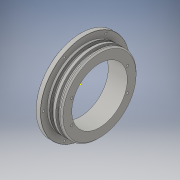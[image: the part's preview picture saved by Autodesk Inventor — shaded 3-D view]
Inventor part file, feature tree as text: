
AUTODESK INVENTOR PART (.ipt)
format: ipt  version: 2016 (Build 200138000, 138)  size: 337,408 bytes
history: native  units: in
note: dims shown in document units (in); Inventor stores cm internally (conversion verified against a paired STEP export)
features: sketch x5, extrude x3, chamfer x2, revolve x1, hole x1
ambient origin geometry x8: Origin, YZ Plane, XZ Plane, XY Plane, X Axis, Y Axis, Z Axis, Center Point
bodies: Solid1 (feature_tree)
feature tree (12):
  revolve  "Revolution1"  [1 undecoded]
  extrude  "Extrusion1"  Depth=0.13in
  extrude  "Extrusion2"  Depth=0.24in
  chamfer  "Chamfer1"  Distance=0.24in
  hole  "Hole1"  [1 undecoded]
  chamfer  "Chamfer2"  Distance=0.125in
  sketch  "Sketch8"  dims[d22=0.139in d23=0.0in d32=0.07in d33=0.125in d34=45.0deg]
  extrude  "Extrusion4"  Depth=0.995in
  sketch  "Sketch2"  dims[d2=0.175in d3=0.14in]
  sketch  "Sketch3"  dims[d4=0.175in d5=0.13in]
  sketch  "Sketch5"  dims[d8=90.0deg d10=4.65in d11=0.24in d12=0.0in]
  sketch  "Sketch9"  dims[d38=0.5in d42=0.125in d43=4.35in d44=2.3622in d46=360.0deg d48=0.1181in d49=0.75in d50=0.375in d51=0.25in d52=0.5635in d53=1.0in d54=0.8108in d55=0.01in d56=0.125in d57=45.0deg d62=3.819in d65=0.15in d66=0.15in d67=0.15in d68=0.055in d71=0.755in d72=1.68in d73=0.3in d74=0.3in d78=0.1181in d79=0.1181in d83=0.1181in d84=0.1181in d85=0.995in d86=0.0in]
note: 2 required parameter values undecoded (feature->parameter linkage not recoverable at this tier; creation-order binding heuristic only, values carry confidence <= 0.55)